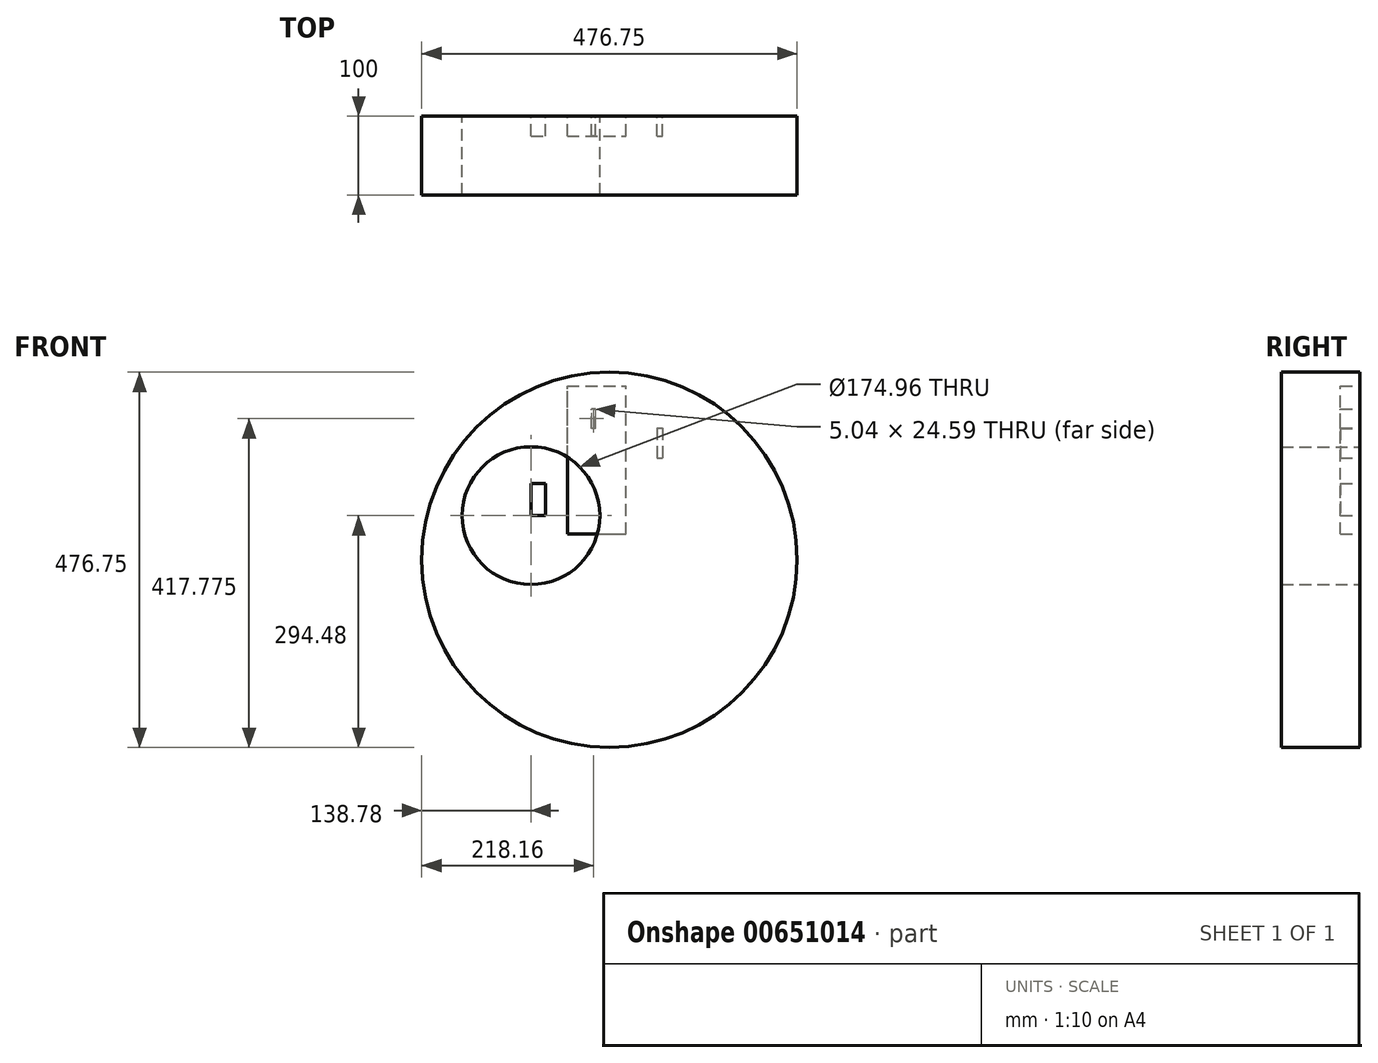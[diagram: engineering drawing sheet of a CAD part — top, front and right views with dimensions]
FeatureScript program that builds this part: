
annotation { "Feature Type Name" : "Feature", "Feature Type Description" : "" }
export const myFeature = defineFeature(function(context is Context, id is Id, definition is map)
    precondition{}
    {
        {
            var Q0;
            Q0=qCreatedBy(makeId("Front.planeOp"),FACE);
            var sketch = newSketch(context, id + "F0", { "sketchPlane" : qUnion([Q0])});
            skLineSegment(sketch, "E0.bottom", {"start": v(0, 41.1) * mm, "end": v(18.48, 41.1) * mm});
            skLineSegment(sketch, "E0.top", {"start": v(0, 0) * mm, "end": v(18.48, 0) * mm});
            skLineSegment(sketch, "E0.left", {"start": v(0, 41.1) * mm, "end": v(0, 0) * mm});
            skLineSegment(sketch, "E0.right", {"start": v(18.48, 41.1) * mm, "end": v(18.48, 0) * mm});
            skLineSegment(sketch, "E1.bottom", {"start": v(81.9, 111) * mm, "end": v(76.86, 111) * mm});
            skLineSegment(sketch, "E1.top", {"start": v(81.9, 135.59) * mm, "end": v(76.86, 135.59) * mm});
            skLineSegment(sketch, "E1.left", {"start": v(81.9, 111) * mm, "end": v(81.9, 135.59) * mm});
            skLineSegment(sketch, "E1.right", {"start": v(76.86, 111) * mm, "end": v(76.86, 135.59) * mm});
            skLineSegment(sketch, "E2.bottom", {"start": v(46.25, -23.35) * mm, "end": v(120.69, -23.35) * mm});
            skLineSegment(sketch, "E2.top", {"start": v(46.25, 164.96) * mm, "end": v(120.69, 164.96) * mm});
            skLineSegment(sketch, "E2.left", {"start": v(46.25, -23.35) * mm, "end": v(46.25, 164.96) * mm});
            skLineSegment(sketch, "E2.right", {"start": v(120.69, -23.35) * mm, "end": v(120.69, 164.96) * mm});
            skLineSegment(sketch, "E3.bottom", {"start": v(159.99, 111.22) * mm, "end": v(166.76, 111.22) * mm});
            skLineSegment(sketch, "E3.top", {"start": v(159.99, 73.45) * mm, "end": v(166.76, 73.45) * mm});
            skLineSegment(sketch, "E3.left", {"start": v(159.99, 111.22) * mm, "end": v(159.99, 73.45) * mm});
            skLineSegment(sketch, "E3.right", {"start": v(166.76, 111.22) * mm, "end": v(166.76, 73.45) * mm});
            skSolve(sketch);
        }
        {
            var Q0;
            Q0 = qSketchRegion(id + "F0", true);
            extrude(context, id + "F1", {"entities" : qUnion([Q0]), "depth" : 25 * mm, "offsetDistance" : 25 * mm});
        }
        {
            var Q0;
            Q0=qCreatedBy(makeId("Front.planeOp"),FACE);
            var sketch = newSketch(context, id + "F2", { "sketchPlane" : qUnion([Q0])});
            skCircle(sketch, "E4", {"center": v(0, 0) * mm, "radius": 87.48 * mm});
            skCircle(sketch, "E5", {"center": v(99.6, -56.1) * mm, "radius": 238.38 * mm});
            skSolve(sketch);
        }
        {
            var Q0;
            Q0 = qSketchRegion(id + "F2", true);
            extrude(context, id + "F3", {"entities" : qUnion([Q0]), "depth" : 100 * mm, "offsetDistance" : 25 * mm});
        }
    });
